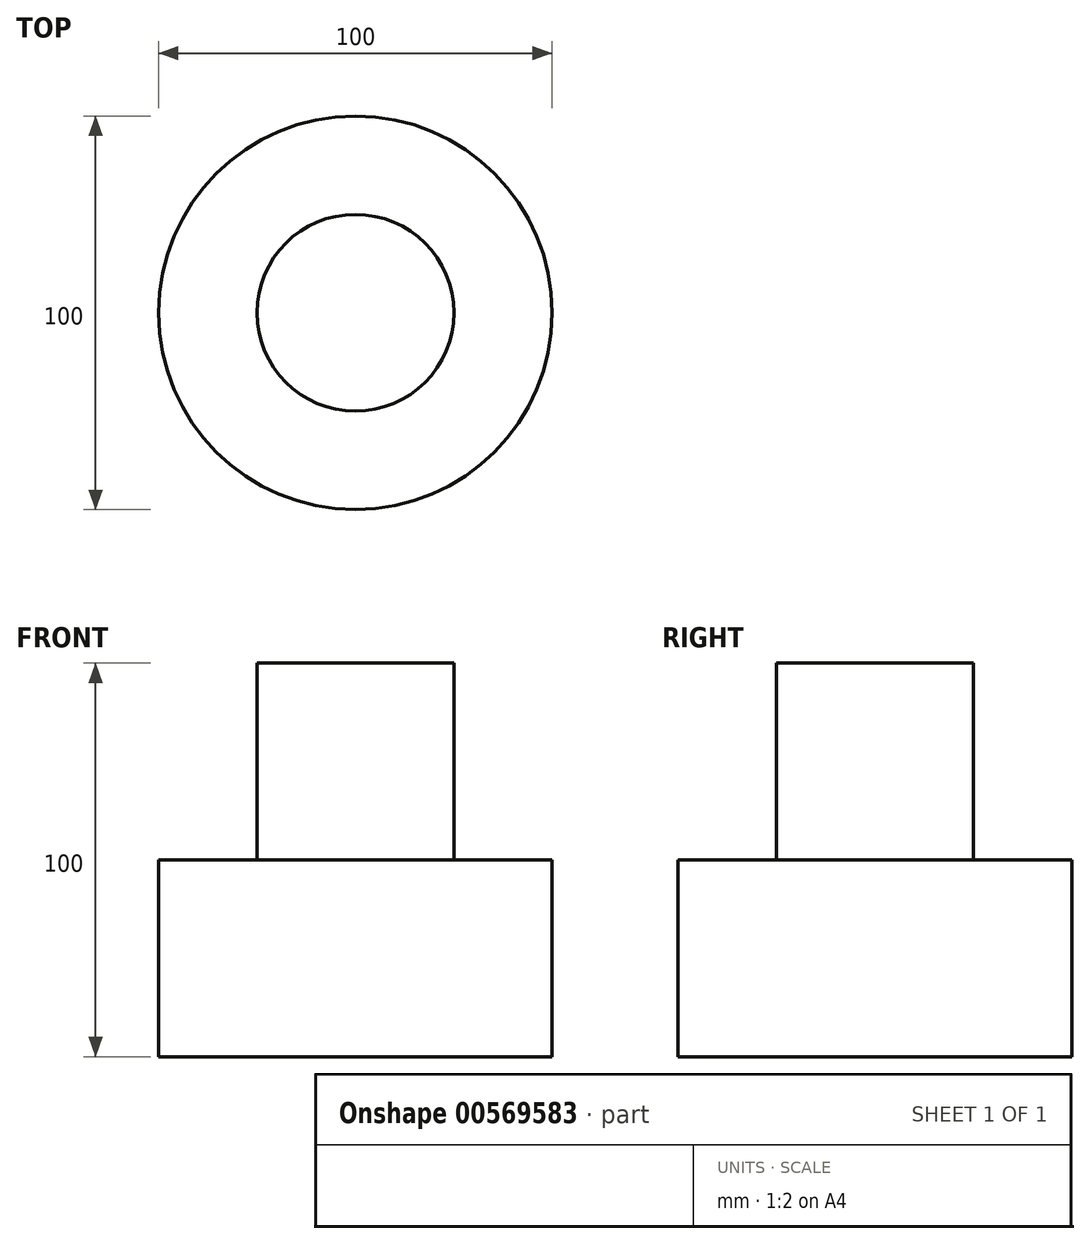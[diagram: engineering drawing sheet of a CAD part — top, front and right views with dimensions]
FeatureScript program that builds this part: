
annotation { "Feature Type Name" : "Feature", "Feature Type Description" : "" }
export const myFeature = defineFeature(function(context is Context, id is Id, definition is map)
    precondition{}
    {
        {
            var Q0;
            Q0=qCreatedBy(makeId("Top.planeOp"),FACE);
            var sketch = newSketch(context, id + "F0", { "sketchPlane" : qUnion([Q0])});
            skCircle(sketch, "E0", {"center": v(0, 0) * mm, "radius": 50 * mm});
            skSolve(sketch);
        }
        {
            var Q0;
            Q0=makeQuery(id+"F0.imprint","IMPRINT",FACE,{"disambiguationData":[TD([[makeQuery(id+"F0.imprint","IMPRINT",EDGE,{"derivedFrom":sQuery(id+"F0.wireOp",EDGE,"E0")}),1.0]])]});
            extrude(context, id + "F1", {"entities" : qUnion([Q0]), "depth" : 50 * mm, "offsetDistance" : 25 * mm});
        }
        {
            var Q0;
            Q0=makeQuery(id+"F1.opExtrude","CAP_FACE",FACE,{"disambiguationData":[OSD([sQuery(id+"F0.wireOp",EDGE,"E0")])],"isStart":false});
            var sketch = newSketch(context, id + "F2", { "sketchPlane" : qUnion([Q0])});
            skCircle(sketch, "E1.0", {"center": v(0, 0) * mm, "radius": 50 * mm});
            skCircle(sketch, "E2", {"center": v(0, 0) * mm, "radius": 25 * mm});
            skSolve(sketch);
        }
        {
            var Q0;
            Q0=makeQuery(id+"F2.imprint","IMPRINT",FACE,{"disambiguationData":[TD([[makeQuery(id+"F2.imprint","IMPRINT",EDGE,{"derivedFrom":sQuery(id+"F2.wireOp",EDGE,"E2")}),1.0]])]});
            extrude(context, id + "F3", {"entities" : qUnion([Q0]), "operationType" : NewBodyOperationType.ADD, "depth" : 50 * mm, "offsetDistance" : 25 * mm});
        }
    });
